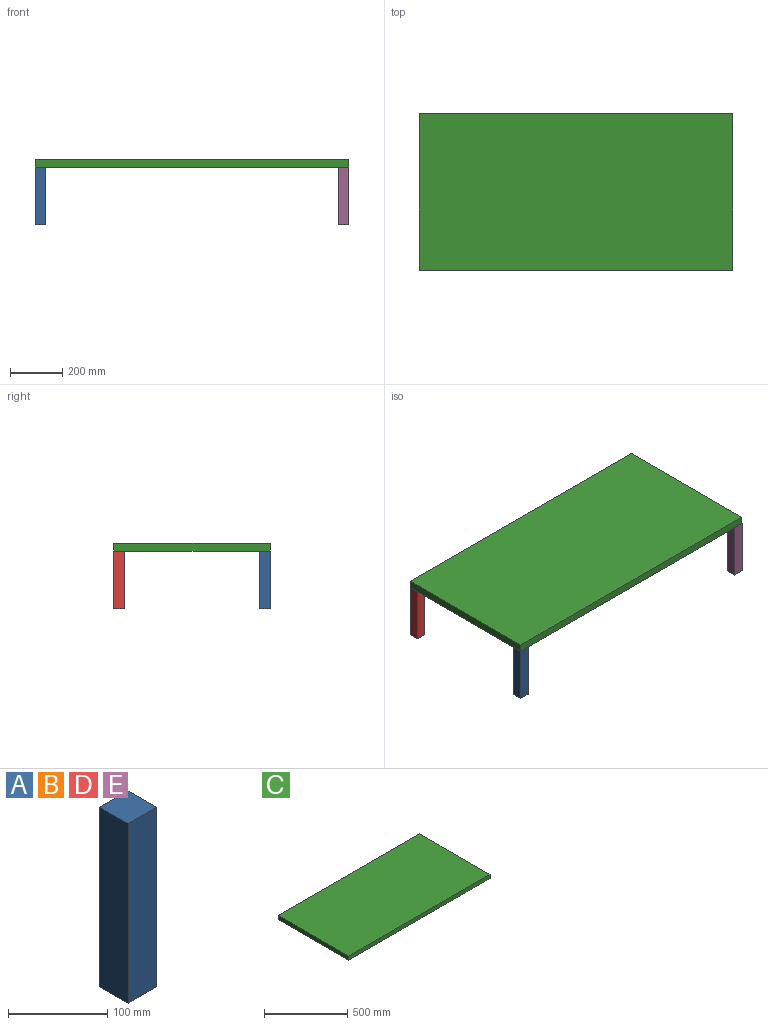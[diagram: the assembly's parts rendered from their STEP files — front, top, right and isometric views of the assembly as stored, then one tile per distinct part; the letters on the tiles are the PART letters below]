
ASSEMBLY  parts=5 mates=13
PART A: 6 faces, bbox 40x40x221.3 mm
  f0: plane 221.26x40mm, normal (0,1,0), area 8850.2mm2, adj f1,f3,f4,f5
  f1: plane 40x40mm, normal (0,0,1), area 1600mm2, adj f0,f2,f4,f5
  f2: plane 221.26x40mm, normal (0,-1,0), area 8850.2mm2, adj f1,f3,f4,f5
  f3: plane 40x40mm, normal (0,0,-1), area 1600mm2, adj f0,f2,f4,f5
  f4: plane 221.26x40mm, normal (1,0,0), area 8850.2mm2, adj f0,f1,f2,f3
  f5: plane 221.26x40mm, normal (-1,0,0), area 8850.2mm2, adj f0,f1,f2,f3
PART B: same geometry as A
PART C: 6 faces, bbox 1200x600x30 mm
  f0: plane 1200x30mm, normal (0,-1,0), area 36000mm2, adj f1,f3,f4,f5
  f1: plane 600x30mm, normal (1,0,0), area 18000mm2, adj f0,f2,f4,f5
  f2: plane 1200x30mm, normal (0,1,0), area 36000mm2, adj f1,f3,f4,f5
  f3: plane 600x30mm, normal (-1,0,0), area 18000mm2, adj f0,f2,f4,f5
  f4: plane 1200x600mm, normal (0,0,1), area 720000mm2, adj f0,f1,f2,f3
  f5: plane 1200x600mm, normal (0,0,-1), area 720000mm2, adj f0,f1,f2,f3
PART D: same geometry as A
PART E: same geometry as A
PLACE A t=(-600,-265.15,-188.47)mm
PLACE B t=(560,294.85,-188.47)mm
PLACE C at identity fixed
PLACE D t=(-600,294.85,-188.47)mm
PLACE E t=(560,-265.15,-188.47)mm
MATE planar C.f5 <-> A.f1  axis (0,0,-1) through (0,0,0)mm
MATE planar C.f2 <-> D.f0  axis (0,1,0) through (0,300,15)mm
MATE planar C.f3 <-> A.f5  axis (-1,0,0) through (-600,0,15)mm
MATE planar C.f2 <-> B.f0  axis (0,1,0) through (0,300,15)mm
MATE planar C.f5 <-> B.f1  axis (0,0,-1) through (0,0,0)mm
MATE planar C.f0 <-> E.f2  axis (0,-1,0) through (0,-300,15)mm
MATE planar D.f1 <-> C.f5  axis (0,0,1) through (-580,280,0)mm
MATE planar C.f1 <-> B.f4  axis (1,0,0) through (600,0,15)mm
MATE planar E.f1 <-> C.f5  axis (0,0,1) through (580,-280,0)mm
MATE planar C.f3 <-> D.f5  axis (-1,0,0) through (-600,0,15)mm
MATE planar C.f0 <-> A.f2  axis (0,-1,0) through (0,-300,15)mm
MATE planar E.f4 <-> C.f1  axis (1,0,0) through (600,-280,0)mm
MATE planar D.f3 <-> D.f1  axis (0,0,-1) through (-580,280,-221.26)mm
